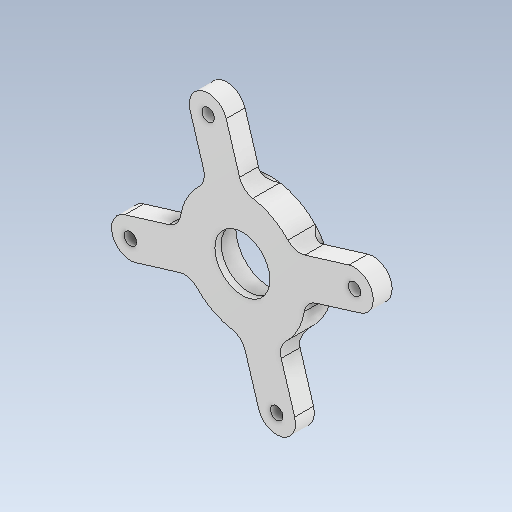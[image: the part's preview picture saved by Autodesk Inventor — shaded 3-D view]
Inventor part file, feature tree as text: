
AUTODESK INVENTOR PART (.ipt)
format: ipt  version: 2020 (Build 240168000, 168)  size: 311,296 bytes
history: native  units: mm
features: sketch x5, extrude x4, projected_geometry x3, other x3, fillet x2, hole x1, reference x1
ambient origin geometry x8: Origin, YZ Plane, XZ Plane, XY Plane, X Axis, Y Axis, Z Axis, Center Point
bodies: Solid1 (feature_tree)
feature tree (19):
  extrude  "Extrusion1"  Depth=9.0mm
  extrude  "Extrusion2"  Depth=3.0mm TaperAngle=0.0deg
  hole  "Hole1"  [1 undecoded]
  extrude  "Extrusion3"  Depth=2.0mm
  fillet  "Fillet1"  Radius=2.0mm
  fillet  "Fillet2"  Radius=4.0mm
  extrude  "Extrusion4"  Depth=1.5mm
  sketch  "Sketch1"  dims[d0=9.0mm d1=9.0mm]
  reference  "Reference1"
  sketch  "Sketch2"  dims[d2=30.0mm d3=3.0mm d4=0.0mm]
  projected_geometry  "Projected Loop1"
  sketch  "Sketch3"  dims[d5=16.15mm d6=3.0mm d7=0.0mm]
  projected_geometry  "Projected Loop2"
  sketch  "Sketch4"  dims[d8=3.0mm d9=6.0mm d10=4.0mm d11=2.0mm d12=90.0deg d13=8.0mm d14=20.594885mm d15=30.0mm d16=2.0mm d17=0.0mm d18=4.0mm]
  sketch  "Sketch5"  dims[d19=2.0mm d23=1.5mm d24=1.5mm d25=0.0mm]
  projected_geometry  "Projected Loop3"
  parser-record x1  (decoder bookkeeping rows leaked as tree rows — omitted from the tree; the rows remain in map.json)
  other  "reducer_3.iam"
  other  "motor_r_1:1"
note: 1 required parameter value undecoded (feature->parameter linkage not recoverable at this tier; creation-order binding heuristic only, values carry confidence <= 0.55)
note: 1 file-system path scrubbed to <path> (originals preserved in map.json)
